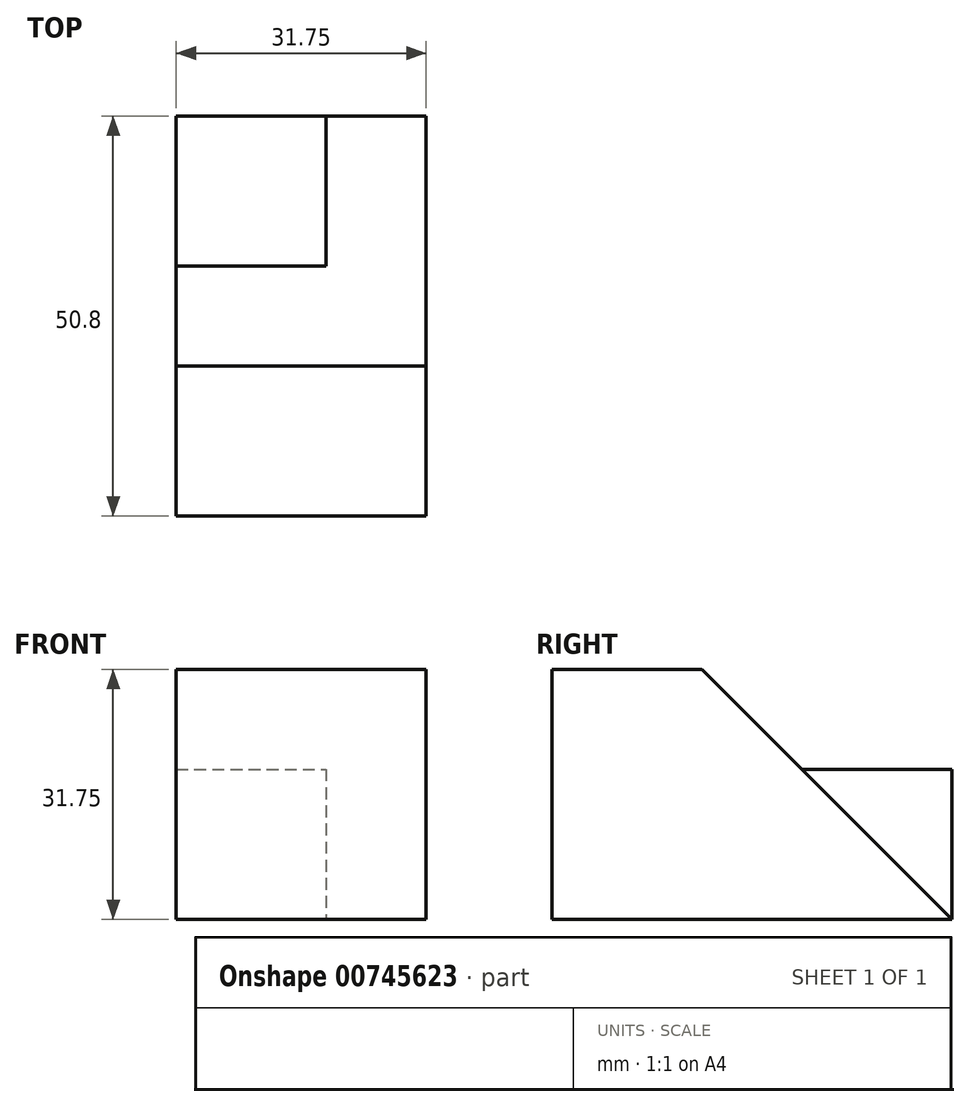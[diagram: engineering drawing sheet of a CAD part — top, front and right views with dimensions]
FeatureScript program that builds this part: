
annotation { "Feature Type Name" : "Feature", "Feature Type Description" : "" }
export const myFeature = defineFeature(function(context is Context, id is Id, definition is map)
    precondition{}
    {
        {
            var Q0;
            Q0=qCreatedBy(makeId("Front.planeOp"),FACE);
            var sketch = newSketch(context, id + "F0", { "sketchPlane" : qUnion([Q0])});
            skLineSegment(sketch, "E0", {"start": v(0, 0) * mm, "end": v(0, 31.75) * mm});
            skLineSegment(sketch, "E1", {"start": v(0, 31.75) * mm, "end": v(31.75, 31.75) * mm});
            skLineSegment(sketch, "E2", {"start": v(31.75, 31.75) * mm, "end": v(31.75, 0) * mm});
            skLineSegment(sketch, "E3", {"start": v(31.75, 0) * mm, "end": v(0, 0) * mm});
            skSolve(sketch);
        }
        {
            var Q0;
            Q0=makeQuery(id+"F0.imprint","IMPRINT",FACE,{"disambiguationData":[TD([[makeQuery(id+"F0.imprint","IMPRINT",EDGE,{"derivedFrom":sQuery(id+"F0.wireOp",EDGE,"E0")}),-1.0]])]});
            extrude(context, id + "F1", {"entities" : qUnion([Q0]), "depth" : 50.8 * mm, "offsetDistance" : 25.4 * mm});
        }
        {
            var Q0;
            Q0=makeQuery(id+"F1.opExtrude","SWEPT_FACE",FACE,{"disambiguationData":[OSD([sQuery(id+"F0.wireOp",EDGE,"E2")])]});
            var sketch = newSketch(context, id + "F2", { "sketchPlane" : qUnion([Q0])});
            skLineSegment(sketch, "E4", {"start": v(-31.75, 31.75) * mm, "end": v(0, 0) * mm});
            skSolve(sketch);
        }
        {
            var Q0;
            {var subQ0=sQuery(id+"F2.wireOp",EDGE,"E4");Q0=makeQuery(id+"F2.imprint","IMPRINT",FACE,{"disambiguationData":[TD([[makeQuery(id+"F2.imprint","IMPRINT",EDGE,{"derivedFrom":subQ0}),1.0]])]});}
            extrude(context, id + "F3", {"entities" : qUnion([Q0]), "operationType" : NewBodyOperationType.REMOVE, "oppositeDirection" : true, "depth" : 12.7 * mm, "offsetDistance" : 25.4 * mm});
        }
        {
            var Q0;
            Q0=makeQuery(id+"F3.boolean.opBoolean","COPY",FACE,{"derivedFrom":makeQuery(id+"F3.opExtrude","CAP_FACE",FACE,{"disambiguationData":[OSD([sQuery(id+"F0.wireOp",EDGE,"E1"),sQuery(id+"F0.wireOp",EDGE,"E2"),sQuery(id+"F2.wireOp",EDGE,"E4")])],"isStart":false})});
            var sketch = newSketch(context, id + "F4", { "sketchPlane" : qUnion([Q0])});
            skLineSegment(sketch, "E5", {"start": v(0, 0) * mm, "end": v(0, 19.06) * mm});
            skLineSegment(sketch, "E6", {"start": v(0, 19.06) * mm, "end": v(-19.06, 19.06) * mm});
            skSolve(sketch);
        }
        {
            var Q0;
            {var subQ0=sQuery(id+"F4.wireOp",EDGE,"E6");Q0=makeQuery(id+"F4.imprint","IMPRINT",FACE,{"disambiguationData":[TD([[makeQuery(id+"F4.imprint","IMPRINT",EDGE,{"derivedFrom":subQ0}),-1.0]])]});}
            extrude(context, id + "F5", {"entities" : qUnion([Q0]), "operationType" : NewBodyOperationType.REMOVE, "endBound" : BoundingType.THROUGH_ALL, "oppositeDirection" : true, "depth" : 25.4 * mm, "offsetDistance" : 25.4 * mm});
        }
    });
